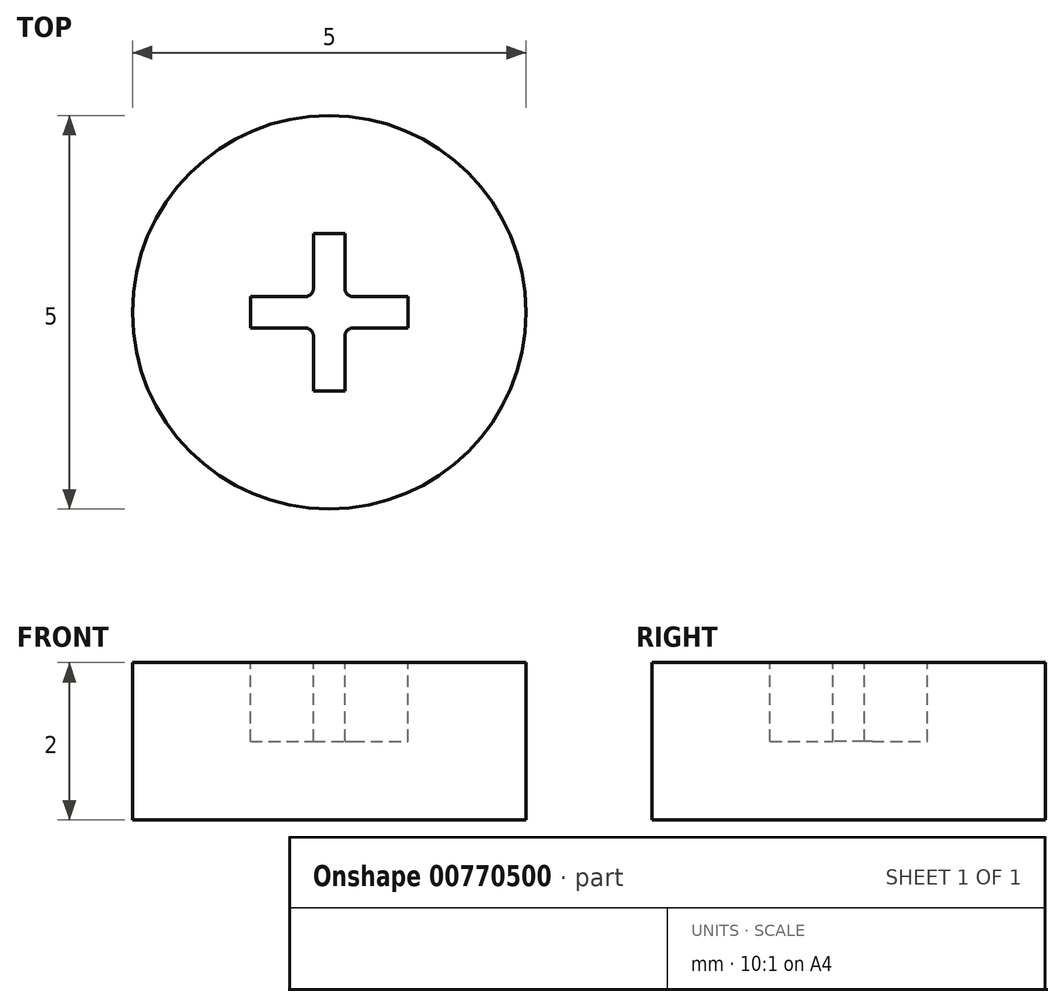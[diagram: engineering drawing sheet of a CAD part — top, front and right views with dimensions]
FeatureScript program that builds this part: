
annotation { "Feature Type Name" : "Feature", "Feature Type Description" : "" }
export const myFeature = defineFeature(function(context is Context, id is Id, definition is map)
    precondition{}
    {
        {
            var Q0;
            Q0=qCreatedBy(makeId("Top.planeOp"),FACE);
            var sketch = newSketch(context, id + "F0", { "sketchPlane" : qUnion([Q0])});
            skCircle(sketch, "E0", {"center": v(0, 0) * mm, "radius": 2.5 * mm});
            skSolve(sketch);
        }
        {
            var Q0;
            Q0=makeQuery(id+"F0.imprint","IMPRINT",FACE,{"disambiguationData":[TD([[makeQuery(id+"F0.imprint","IMPRINT",EDGE,{"derivedFrom":sQuery(id+"F0.wireOp",EDGE,"E0")}),1.0]])]});
            extrude(context, id + "F1", {"entities" : qUnion([Q0]), "depth" : 2 * mm, "offsetDistance" : 25 * mm});
        }
        {
            var Q0;
            Q0=makeQuery(id+"F1.opExtrude","CAP_FACE",FACE,{"disambiguationData":[OSD([sQuery(id+"F0.wireOp",EDGE,"E0")])],"isStart":false});
            var sketch = newSketch(context, id + "F2", { "sketchPlane" : qUnion([Q0])});
            skLineSegment(sketch, "E1.bottom", {"start": v(-0.2, -1) * mm, "end": v(0.2, -1) * mm});
            skLineSegment(sketch, "E1.top", {"start": v(-0.2, 1) * mm, "end": v(0.2, 1) * mm});
            skLineSegment(sketch, "E1.left", {"start": v(-0.2, -1) * mm, "end": v(-0.2, -0.3) * mm});
            skLineSegment(sketch, "E1.right", {"start": v(0.2, -1) * mm, "end": v(0.2, -0.3) * mm});
            skLineSegment(sketch, "E2.bottom", {"start": v(-1, 0.2) * mm, "end": v(-0.3, 0.2) * mm});
            skLineSegment(sketch, "E2.top", {"start": v(-1, -0.2) * mm, "end": v(-0.3, -0.2) * mm});
            skLineSegment(sketch, "E2.left", {"start": v(-1, 0.2) * mm, "end": v(-1, -0.2) * mm});
            skLineSegment(sketch, "E2.right", {"start": v(1, 0.2) * mm, "end": v(1, -0.2) * mm});
            skLineSegment(sketch, "E3.trimOffspring", {"start": v(-0.2, 0.3) * mm, "end": v(-0.2, 1) * mm});
            skLineSegment(sketch, "E4.trimOffspring", {"start": v(0.3, 0.2) * mm, "end": v(1, 0.2) * mm});
            skLineSegment(sketch, "E5.trimOffspring", {"start": v(0.2, 0.3) * mm, "end": v(0.2, 1) * mm});
            skLineSegment(sketch, "E6.trimOffspring", {"start": v(0.3, -0.2) * mm, "end": v(1, -0.2) * mm});
            skPoint(sketch, "E7.visualSharp", {"position": v(-0.2, 0.2) * mm});
            skArc(sketch, "E7.filletArc", {"start": v(-0.3, 0.2) * mm, "mid": v(-0.23, 0.23) * mm, "end": v(-0.2, 0.3) * mm});
            skPoint(sketch, "E8.visualSharp", {"position": v(0.2, 0.2) * mm});
            skArc(sketch, "E8.filletArc", {"start": v(0.2, 0.3) * mm, "mid": v(0.23, 0.23) * mm, "end": v(0.3, 0.2) * mm});
            skPoint(sketch, "E9.visualSharp", {"position": v(0.2, -0.2) * mm});
            skArc(sketch, "E9.filletArc", {"start": v(0.3, -0.2) * mm, "mid": v(0.23, -0.23) * mm, "end": v(0.2, -0.3) * mm});
            skPoint(sketch, "E10.visualSharp", {"position": v(-0.2, -0.2) * mm});
            skArc(sketch, "E10.filletArc", {"start": v(-0.2, -0.3) * mm, "mid": v(-0.23, -0.23) * mm, "end": v(-0.3, -0.2) * mm});
            skSolve(sketch);
        }
        {
            var Q0;
            Q0 = qSketchRegion(id + "F2", true);
            extrude(context, id + "F3", {"entities" : qUnion([Q0]), "operationType" : NewBodyOperationType.REMOVE, "oppositeDirection" : true, "depth" : 1 * mm, "offsetDistance" : 25 * mm});
        }
    });
